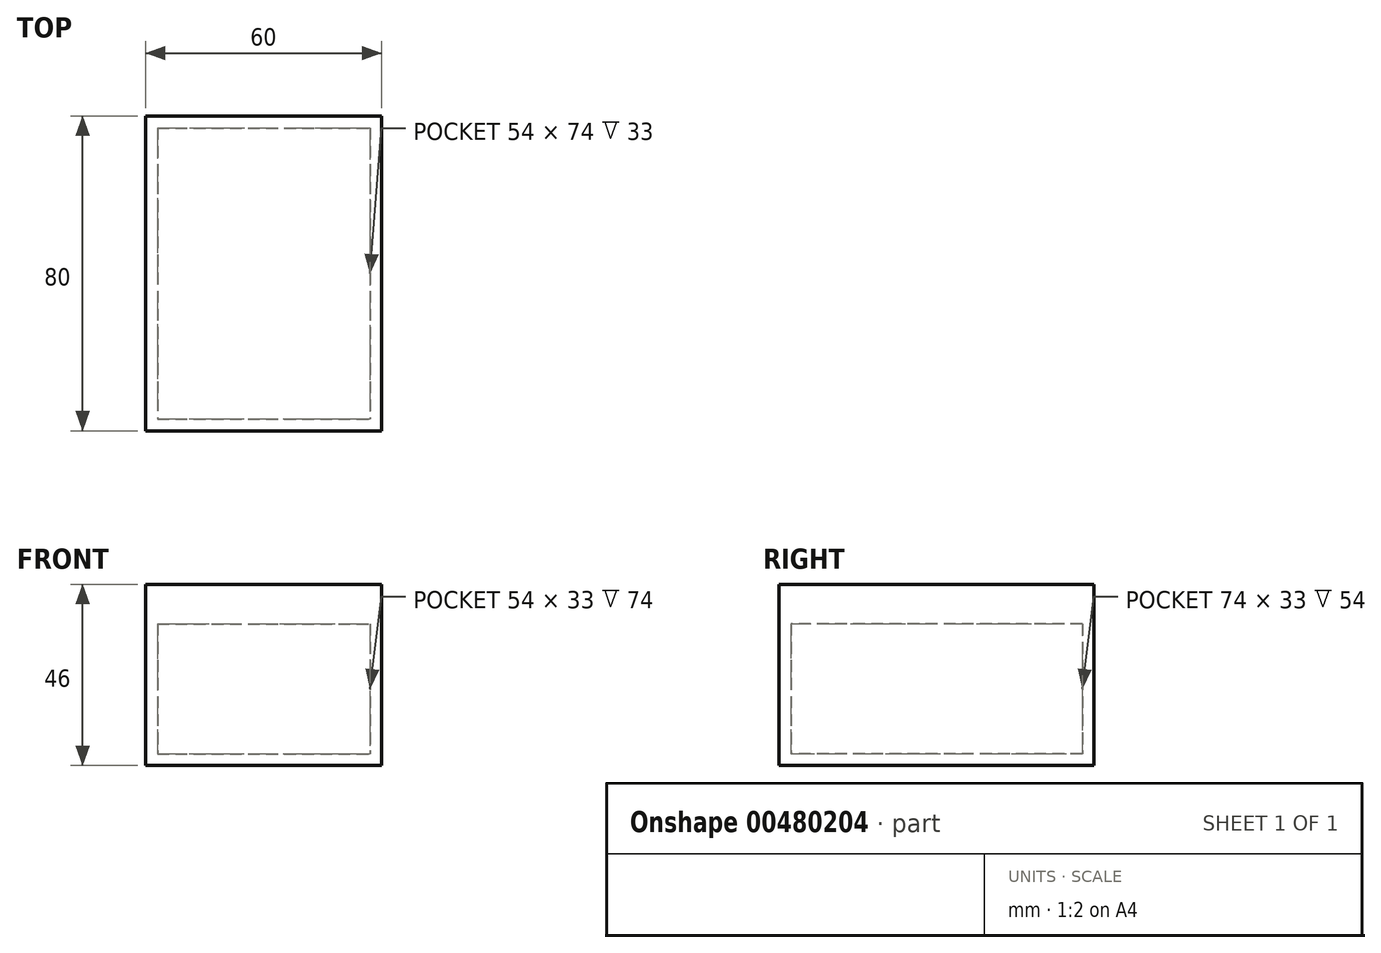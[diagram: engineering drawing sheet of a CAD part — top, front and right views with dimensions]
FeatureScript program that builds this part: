
annotation { "Feature Type Name" : "Feature", "Feature Type Description" : "" }
export const myFeature = defineFeature(function(context is Context, id is Id, definition is map)
    precondition{}
    {
        {
            var Q0;
            Q0=qCreatedBy(makeId("Top.planeOp"),FACE);
            var sketch = newSketch(context, id + "F0", { "sketchPlane" : qUnion([Q0])});
            skLineSegment(sketch, "E0.bottom", {"start": v(-30, 40) * mm, "end": v(30, 40) * mm});
            skLineSegment(sketch, "E0.top", {"start": v(-30, -40) * mm, "end": v(30, -40) * mm});
            skLineSegment(sketch, "E0.left", {"start": v(-30, 40) * mm, "end": v(-30, -40) * mm});
            skLineSegment(sketch, "E0.right", {"start": v(30, 40) * mm, "end": v(30, -40) * mm});
            skPoint(sketch, "E0.middle", {"position": v(0, 0) * mm});
            skSolve(sketch);
        }
        {
            var Q0;
            Q0=makeQuery(id+"F0.imprint","IMPRINT",FACE,{"disambiguationData":[TD([[makeQuery(id+"F0.imprint","IMPRINT",EDGE,{"derivedFrom":sQuery(id+"F0.wireOp",EDGE,"E0.bottom")}),-1.0]])]});
            extrude(context, id + "F1", {"entities" : qUnion([Q0]), "depth" : 40 * mm});
        }
        {
            var Q0;
            Q0=makeQuery(id+"F1.opExtrude","CAP_FACE",FACE,{"disambiguationData":[OSD([sQuery(id+"F0.wireOp",EDGE,"E0.bottom"),sQuery(id+"F0.wireOp",EDGE,"E0.top"),sQuery(id+"F0.wireOp",EDGE,"E0.left"),sQuery(id+"F0.wireOp",EDGE,"E0.right")])],"isStart":false});
            shell(context, id + "F2", {"entities" : qUnion([Q0]), "thickness" : 3 * mm});
        }
        {
            var Q0;
            Q0=makeQuery(id+"F1.opExtrude","CAP_FACE",FACE,{"disambiguationData":[OSD([sQuery(id+"F0.wireOp",EDGE,"E0.bottom"),sQuery(id+"F0.wireOp",EDGE,"E0.top"),sQuery(id+"F0.wireOp",EDGE,"E0.left"),sQuery(id+"F0.wireOp",EDGE,"E0.right")])],"isStart":false});
            var sketch = newSketch(context, id + "F3", { "sketchPlane" : qUnion([Q0])});
            skLineSegment(sketch, "E1.bottom", {"start": v(-30, 40) * mm, "end": v(30, 40) * mm});
            skLineSegment(sketch, "E1.top", {"start": v(-30, -40) * mm, "end": v(30, -40) * mm});
            skLineSegment(sketch, "E1.left", {"start": v(-30, 40) * mm, "end": v(-30, -40) * mm});
            skLineSegment(sketch, "E1.right", {"start": v(30, 40) * mm, "end": v(30, -40) * mm});
            skSolve(sketch);
        }
        {
            var Q0;
            Q0=makeQuery(id+"F3.imprint","IMPRINT",FACE,{"disambiguationData":[TD([[makeQuery(id+"F3.imprint","IMPRINT",EDGE,{"derivedFrom":sQuery(id+"F3.wireOp",EDGE,"E1.bottom")}),-1.0]])]});
            var Q1;
            {var subQ0=sQuery(id+"F0.wireOp",EDGE,"E0.bottom");Q1=makeQuery(id+"F3.imprint","IMPRINT",FACE,{"disambiguationData":[TD([[makeQuery(id+"F3.imprint","IMPRINT",EDGE,{"derivedFrom":makeQuery(id+"F2.opShell","OFFSET_EDGE",EDGE,{"disambiguationData":[OSD([subQ0]),TDD([makeQuery(id+"F1.opExtrude","CAP_EDGE",EDGE,{"disambiguationData":[OSD([subQ0])],"isStart":false})])]})}),-1.0]])]});}
            extrude(context, id + "F4", {"entities" : qUnion([Q0, Q1]), "depth" : 3 * mm});
        }
        {
            var Q0;
            Q0=makeQuery(id+"F4.opExtrude","CAP_FACE",FACE,{"disambiguationData":[OSD([sQuery(id+"F3.wireOp",EDGE,"E1.bottom"),sQuery(id+"F3.wireOp",EDGE,"E1.top"),sQuery(id+"F3.wireOp",EDGE,"E1.left"),sQuery(id+"F3.wireOp",EDGE,"E1.right")])],"isStart":false});
            extrude(context, id + "F5", {"entities" : qUnion([Q0]), "operationType" : NewBodyOperationType.ADD, "depth" : 3 * mm});
        }
        {
            var Q0;
            {var subQ0=sQuery(id+"F0.wireOp",EDGE,"E0.bottom");Q0=makeQuery(id+"F3.imprint","IMPRINT",FACE,{"disambiguationData":[TD([[makeQuery(id+"F3.imprint","IMPRINT",EDGE,{"derivedFrom":makeQuery(id+"F2.opShell","OFFSET_EDGE",EDGE,{"disambiguationData":[OSD([subQ0]),TDD([makeQuery(id+"F1.opExtrude","CAP_EDGE",EDGE,{"disambiguationData":[OSD([subQ0])],"isStart":false})])]})}),-1.0]])]});}
            extrude(context, id + "F6", {"entities" : qUnion([Q0]), "operationType" : NewBodyOperationType.ADD, "oppositeDirection" : true, "depth" : 4 * mm});
        }
        {
            var Q0;
            Q0=makeQuery(id+"F0.imprint","IMPRINT",FACE,{"disambiguationData":[TD([[makeQuery(id+"F0.imprint","IMPRINT",EDGE,{"derivedFrom":sQuery(id+"F0.wireOp",EDGE,"E0.bottom")}),-1.0]])]});
            var sketch = newSketch(context, id + "F7", { "sketchPlane" : qUnion([Q0])});
            skCircle(sketch, "E2", {"center": v(-20, 30) * mm, "radius": 1.5 * mm});
            skCircle(sketch, "E3", {"center": v(20, 30) * mm, "radius": 1.5 * mm});
            skCircle(sketch, "E4", {"center": v(-7.58, -2.73) * mm, "radius": 1.5 * mm});
            skCircle(sketch, "E5", {"center": v(2.57, -2.4) * mm, "radius": 1.5 * mm});
            skCircle(sketch, "E6", {"center": v(-15.07, 22.9) * mm, "radius": 6.6 * mm});
            skCircle(sketch, "E7", {"center": v(-10.01, 16.26) * mm, "radius": 20.94 * mm});
            skCircle(sketch, "E8", {"center": v(-10.01, 16.26) * mm, "radius": 7.43 * mm});
            skCircle(sketch, "E9", {"center": v(-28.35, 6.16) * mm, "radius": 24.8 * mm});
            skSolve(sketch);
        }
        {
            var Q0;
            Q0=sQuery(id+"F7.wireOp",EDGE,"E3");
            extrude(context, id + "F8", {"bodyType" : ToolBodyType.SURFACE, "surfaceEntities" : qUnion([Q0]), "depth" : 25 * mm});
        }
        {
            var Q0;
            Q0=sQuery(id+"F7.wireOp",EDGE,"E2");
            extrude(context, id + "F9", {"bodyType" : ToolBodyType.SURFACE, "surfaceEntities" : qUnion([Q0]), "depth" : 25 * mm});
        }
        {
            var Q0;
            Q0=sQuery(id+"F7.wireOp",EDGE,"E5");
            extrude(context, id + "F10", {"bodyType" : ToolBodyType.SURFACE, "surfaceEntities" : qUnion([Q0]), "depth" : 25 * mm});
        }
        {
            var Q0;
            Q0=sQuery(id+"F7.wireOp",EDGE,"E4");
            extrude(context, id + "F11", {"bodyType" : ToolBodyType.SURFACE, "surfaceEntities" : qUnion([Q0]), "depth" : 25 * mm});
        }
    });
